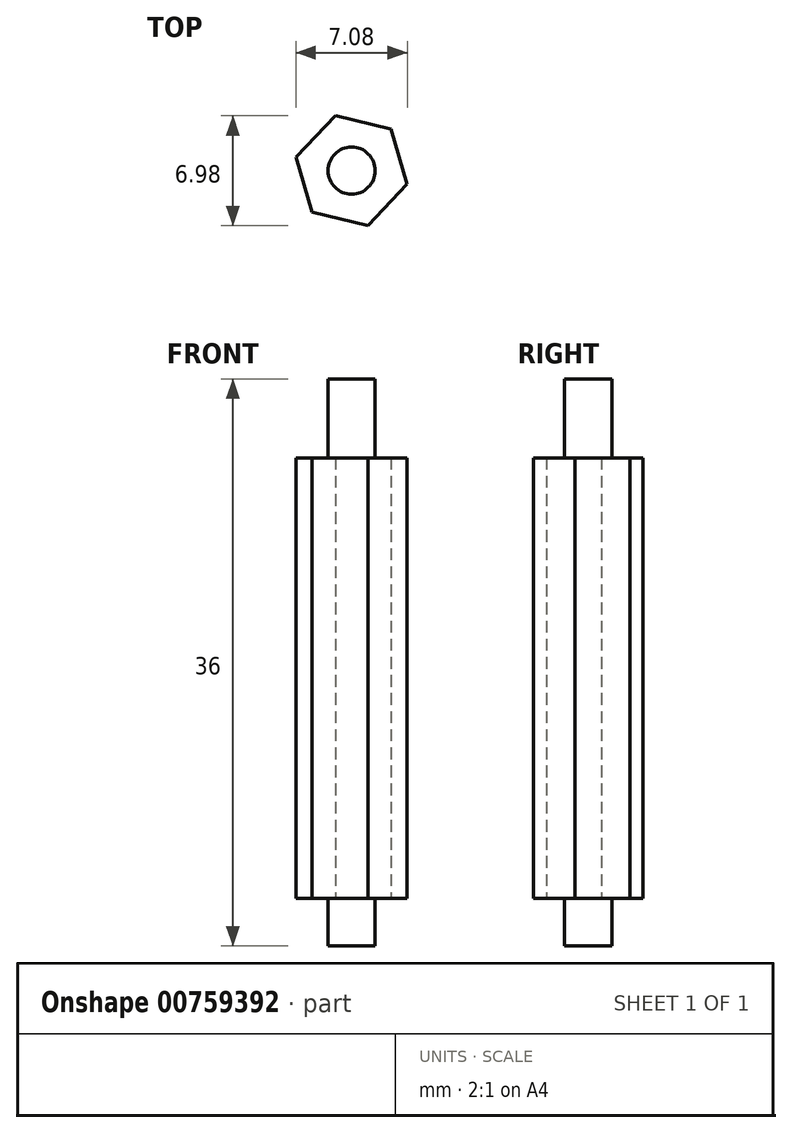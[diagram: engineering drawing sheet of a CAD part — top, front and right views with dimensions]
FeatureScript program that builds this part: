
annotation { "Feature Type Name" : "Feature", "Feature Type Description" : "" }
export const myFeature = defineFeature(function(context is Context, id is Id, definition is map)
    precondition{}
    {
        {
            var Q0;
            Q0=qCreatedBy(makeId("Top.planeOp"),FACE);
            var sketch = newSketch(context, id + "F0", { "sketchPlane" : qUnion([Q0])});
            skCircle(sketch, "E0.cCircle", {"center": v(0, 0) * mm, "radius": 3.15 * mm, "construction": true});
            skLineSegment(sketch, "E0.0", {"start": v(-3.54, 0.85) * mm, "end": v(-1.03, 3.49) * mm});
            skLineSegment(sketch, "E0.1", {"start": v(-1.03, 3.49) * mm, "end": v(2.5, 2.64) * mm});
            skLineSegment(sketch, "E0.2", {"start": v(2.5, 2.64) * mm, "end": v(3.54, -0.85) * mm});
            skLineSegment(sketch, "E0.3", {"start": v(3.54, -0.85) * mm, "end": v(1.03, -3.49) * mm});
            skLineSegment(sketch, "E0.4", {"start": v(1.03, -3.49) * mm, "end": v(-2.5, -2.64) * mm});
            skLineSegment(sketch, "E0.5", {"start": v(-2.5, -2.64) * mm, "end": v(-3.54, 0.85) * mm});
            skPoint(sketch, "E0.0.midPoint", {"position": v(-2.28, 2.17) * mm});
            skSolve(sketch);
        }
        {
            var Q0;
            Q0=makeQuery(id+"F0.imprint","IMPRINT",FACE,{"disambiguationData":[TD([[makeQuery(id+"F0.imprint","IMPRINT",EDGE,{"derivedFrom":sQuery(id+"F0.wireOp",EDGE,"E0.0")}),-1.0]])]});
            extrude(context, id + "F1", {"entities" : qUnion([Q0]), "depth" : 28 * mm, "offsetDistance" : 25 * mm});
        }
        {
            var Q0;
            Q0=makeQuery(id+"F1.opExtrude","CAP_FACE",FACE,{"disambiguationData":[OSD([sQuery(id+"F0.wireOp",EDGE,"E0.0"),sQuery(id+"F0.wireOp",EDGE,"E0.1"),sQuery(id+"F0.wireOp",EDGE,"E0.2"),sQuery(id+"F0.wireOp",EDGE,"E0.3"),sQuery(id+"F0.wireOp",EDGE,"E0.4"),sQuery(id+"F0.wireOp",EDGE,"E0.5")])],"isStart":false});
            var sketch = newSketch(context, id + "F2", { "sketchPlane" : qUnion([Q0])});
            skCircle(sketch, "E1", {"center": v(0, 0) * mm, "radius": 1.5 * mm});
            skSolve(sketch);
        }
        {
            var Q0;
            Q0=makeQuery(id+"F2.imprint","IMPRINT",FACE,{"disambiguationData":[TD([[makeQuery(id+"F2.imprint","IMPRINT",EDGE,{"derivedFrom":sQuery(id+"F2.wireOp",EDGE,"E1")}),1.0]])]});
            extrude(context, id + "F3", {"entities" : qUnion([Q0]), "operationType" : NewBodyOperationType.ADD, "depth" : 5 * mm, "offsetDistance" : 25 * mm});
        }
        {
            var Q0;
            Q0=makeQuery(id+"F1.opExtrude","CAP_FACE",FACE,{"disambiguationData":[OSD([sQuery(id+"F0.wireOp",EDGE,"E0.0"),sQuery(id+"F0.wireOp",EDGE,"E0.1"),sQuery(id+"F0.wireOp",EDGE,"E0.2"),sQuery(id+"F0.wireOp",EDGE,"E0.3"),sQuery(id+"F0.wireOp",EDGE,"E0.4"),sQuery(id+"F0.wireOp",EDGE,"E0.5")])],"isStart":true});
            var sketch = newSketch(context, id + "F4", { "sketchPlane" : qUnion([Q0])});
            skCircle(sketch, "E2", {"center": v(0, 0) * mm, "radius": 1.5 * mm});
            skSolve(sketch);
        }
        {
            var Q0;
            Q0=makeQuery(id+"F4.imprint","IMPRINT",FACE,{"disambiguationData":[TD([[makeQuery(id+"F4.imprint","IMPRINT",EDGE,{"derivedFrom":sQuery(id+"F4.wireOp",EDGE,"E2")}),1.0]])]});
            extrude(context, id + "F5", {"entities" : qUnion([Q0]), "operationType" : NewBodyOperationType.ADD, "depth" : 3 * mm, "offsetDistance" : 25 * mm});
        }
    });
